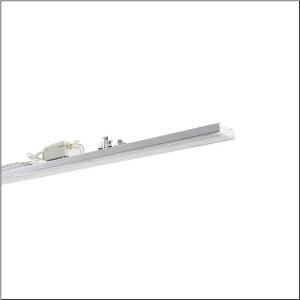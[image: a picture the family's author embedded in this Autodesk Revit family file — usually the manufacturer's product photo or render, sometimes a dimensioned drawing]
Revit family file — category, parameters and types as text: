
# Revit family: licross_21_recessed_ho_52tl11de47xs
name_source: partatom
category: Lighting Fixtures
units: mm (PartAtom-declared; Revit-internal decimal feet)

## family parameters
Cut with Voids When Loaded = No
Host = Face
Light Source = No
Part Type = Normal
Room Calculation Point = No
Round Connector Dimension = Use Diameter
Shared = No

## types (1)
- --- (1 x LED, 7480 lm, 44.1 W, 4000K)
    Apparent Load = 44 VA
    CIE Flux Codes = 87 95 99 100 100
    Color Rendering = 80
    Color Temperature = 4000K
    Default Elevation = 1800 mm
    Description = Licross 21 Recessed HO, luminaire insert, of sheet steel, galvanised, coil coated, white, length: 750mm, width: 66mm, height: 67mm, LED rated luminous flux: 7.480lm, light colour: 840, SDCM (Standard Deviation of Colour Matching)MacAdam ≤ 3 SDCM (initial), control gear: DALI 2, with plug, 5-pole, with phase selection, mains connection: 220..240V, AC, 50/60Hz, rated input power: 44W, internal wiring halogen-free, primary light control with lens, of plastic, primary optical cover: cover, of PMMA, light emission: direct distribution, primary light characteristic: symmetric, protection rating (complete): IP40, insulation class (complete): insulation class I (protective earthing), certification: CE, ENEC, VDE, UKCA, protection symbol: D if used in an environment without relevant dust loads with corresponding accessories, impact resistance: IK06, permissible ambient temperature for indoor applications: -25..+30°C, corresponds to IFS (International Featured Standards) requirements for safety and quality in the food industry, reducing of maximum allowable ambient temperature of 5°C with ceiling mounting, LABS conformity tested according to VDMA 24364:2018-05, The light source and the operating device comply with the requirements of the Ecodesign Regulation (EU) 2019/2020 and are replaceable in accordance with this regulation, packaging unit: 1 piece
    Height = 58 mm
    Lamp = 1 x LED
    Lamp Light Flux = 7480 lm
    Lamp Power = 44.1 W
    Lamp count = 1
    Length = 750 mm
    Luminous efficacy = 170 lm/W
    Manufacturer = Siteco
    ModVariant = No
    Model = 52TL11DE47XS
    Mounting Place = Ceiling
    Mounting Type = Pendant
    Number of Poles = 1
    OnlyDefault = Yes
    Power Factor = 1
    Product Name = Licross 21 Recessed HO
    Product group = luminaire insert | ceiling pendant
    ProductGroupID = 901
    Protection Class = Protection class I
    Protection Degree = IP 40
    RLX_Detail_Level = 1
    RLX_Emergency_Light_Flux = 0 lm
    RLX_Emergency_Type = 0
    RLX_Emergency_Type_DB = No
    RlxData = <blob elided: 29529 chars, md5=27868d28>
    Socket = socket
    Standby Power = 0 W
    System Light Flux = 7480 lm
    System Power = 44 W
    Type Comments = factory setting: luminous flux: 100 % | dim-lin: 254 | 484 mA
    Type Image = l_1296930.jpg
    URL = http://relux.com
    VarID = @adj_129185
    Voltage = 0 V
    Weight = 0.00 kg
    Width = 66 mm

## geometry (parser evidence)
native form markers: Blend x4, Sweep x9
no freeform markers — native parametric forms only
